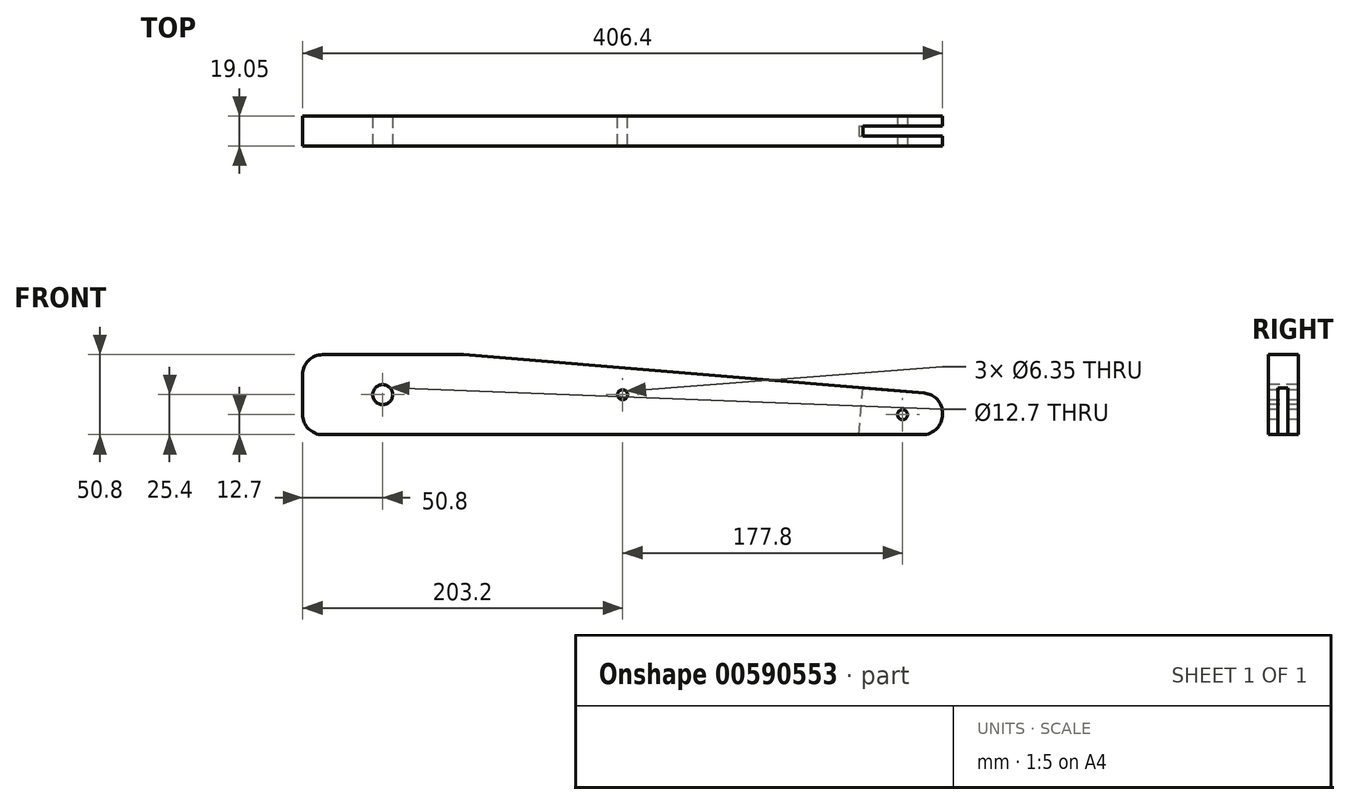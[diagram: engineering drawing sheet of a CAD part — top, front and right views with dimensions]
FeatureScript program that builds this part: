
annotation { "Feature Type Name" : "Feature", "Feature Type Description" : "" }
export const myFeature = defineFeature(function(context is Context, id is Id, definition is map)
    precondition{}
    {
        {
            var Q0;
            Q0=qCreatedBy(makeId("Front.planeOp"),FACE);
            var sketch = newSketch(context, id + "F0", { "sketchPlane" : qUnion([Q0])});
            skLineSegment(sketch, "E0.bottom", {"start": v(-203.2, 25.4) * mm, "end": v(203.2, 25.4) * mm});
            skLineSegment(sketch, "E0.top", {"start": v(-203.2, -25.4) * mm, "end": v(203.2, -25.4) * mm});
            skLineSegment(sketch, "E0.left", {"start": v(-203.2, 25.4) * mm, "end": v(-203.2, -25.4) * mm});
            skLineSegment(sketch, "E0.right", {"start": v(203.2, 25.4) * mm, "end": v(203.2, -25.4) * mm});
            skPoint(sketch, "E0.middle", {"position": v(0, 0) * mm});
            skCircle(sketch, "E1", {"center": v(0, 0) * mm, "radius": 3.18 * mm});
            skSolve(sketch);
        }
        {
            var Q0;
            Q0=makeQuery(id+"F0.imprint","IMPRINT",FACE,{"disambiguationData":[TD([[makeQuery(id+"F0.imprint","IMPRINT",EDGE,{"derivedFrom":sQuery(id+"F0.wireOp",EDGE,"E0.bottom")}),-1.0]])]});
            extrude(context, id + "F1", {"entities" : qUnion([Q0]), "depth" : 19.05 * mm, "offsetDistance" : 25.4 * mm});
        }
        {
            var Q0;
            Q0=makeQuery(id+"F1.opExtrude","SWEPT_EDGE",EDGE,{"disambiguationData":[OSD([sQuery(id+"F0.wireOp",EDGE,"E0.bottom"),sQuery(id+"F0.wireOp",EDGE,"E0.right")])]});
            chamfer(context, id + "F2", {"entities" : qUnion([Q0]), "chamferType" : ChamferType.TWO_OFFSETS, "width1" : 304.8 * mm, "oppositeDirection" : false, "width2" : 25.4 * mm, "tangentPropagation" : true});
        }
        {
            var Q0;
            Q0=makeQuery(id+"F1.opExtrude","CAP_FACE",FACE,{"disambiguationData":[OSD([sQuery(id+"F0.wireOp",EDGE,"E0.bottom"),sQuery(id+"F0.wireOp",EDGE,"E0.top"),sQuery(id+"F0.wireOp",EDGE,"E0.left"),sQuery(id+"F0.wireOp",EDGE,"E0.right")])],"isStart":false});
            var sketch = newSketch(context, id + "F3", { "sketchPlane" : qUnion([Q0])});
            skCircle(sketch, "E2", {"center": v(-152.4, 0) * mm, "radius": 6.35 * mm});
            skPoint(sketch, "E2.centerSnap0", {"position": v(-152.4, 25.4) * mm});
            skSolve(sketch);
        }
        {
            var Q0;
            Q0=makeQuery(id+"F3.imprint","IMPRINT",FACE,{"disambiguationData":[TD([[makeQuery(id+"F3.imprint","IMPRINT",EDGE,{"derivedFrom":sQuery(id+"F3.wireOp",EDGE,"E2")}),1.0]])]});
            extrude(context, id + "F4", {"entities" : qUnion([Q0]), "operationType" : NewBodyOperationType.REMOVE, "endBound" : BoundingType.THROUGH_ALL, "oppositeDirection" : true, "depth" : 25.4 * mm, "offsetDistance" : 25.4 * mm});
        }
        {
            var Q0;
            Q0=makeQuery(id+"F1.opExtrude","CAP_FACE",FACE,{"disambiguationData":[OSD([sQuery(id+"F0.wireOp",EDGE,"E0.bottom"),sQuery(id+"F0.wireOp",EDGE,"E0.top"),sQuery(id+"F0.wireOp",EDGE,"E0.left"),sQuery(id+"F0.wireOp",EDGE,"E0.right")])],"isStart":false});
            var sketch = newSketch(context, id + "F5", { "sketchPlane" : qUnion([Q0])});
            skCircle(sketch, "E3", {"center": v(177.8, -12.7) * mm, "radius": 3.18 * mm});
            skPoint(sketch, "E3.centerSnap0", {"position": v(203.2, -12.7) * mm});
            skSolve(sketch);
        }
        {
            var Q0;
            Q0=makeQuery(id+"F5.imprint","IMPRINT",FACE,{"disambiguationData":[TD([[makeQuery(id+"F5.imprint","IMPRINT",EDGE,{"derivedFrom":sQuery(id+"F5.wireOp",EDGE,"E3")}),1.0]])]});
            extrude(context, id + "F6", {"entities" : qUnion([Q0]), "operationType" : NewBodyOperationType.REMOVE, "endBound" : BoundingType.THROUGH_ALL, "oppositeDirection" : true, "depth" : 25.4 * mm, "offsetDistance" : 25.4 * mm});
        }
        {
            var Q0;
            Q0=makeQuery(id+"F2.opChamfer","BLEND_FACE",FACE,{"disambiguationData":[OSD([sQuery(id+"F0.wireOp",EDGE,"E0.bottom"),sQuery(id+"F0.wireOp",EDGE,"E0.right")])]});
            var sketch = newSketch(context, id + "F7", { "sketchPlane" : qUnion([Q0])});
            skLineSegment(sketch, "E4.bottom", {"start": v(151.7, -6.35) * mm, "end": v(202.5, -6.35) * mm});
            skLineSegment(sketch, "E4.top", {"start": v(151.7, -12.7) * mm, "end": v(202.5, -12.7) * mm});
            skLineSegment(sketch, "E4.left", {"start": v(151.7, -6.35) * mm, "end": v(151.7, -12.7) * mm});
            skLineSegment(sketch, "E4.right", {"start": v(202.5, -6.35) * mm, "end": v(202.5, -12.7) * mm});
            skSolve(sketch);
        }
        {
            var Q0;
            Q0=makeQuery(id+"F7.imprint","IMPRINT",FACE,{"disambiguationData":[TD([[makeQuery(id+"F7.imprint","IMPRINT",EDGE,{"derivedFrom":sQuery(id+"F7.wireOp",EDGE,"E4.bottom")}),-1.0]])]});
            extrude(context, id + "F8", {"entities" : qUnion([Q0]), "operationType" : NewBodyOperationType.REMOVE, "endBound" : BoundingType.THROUGH_ALL, "oppositeDirection" : true, "depth" : 25.4 * mm, "offsetDistance" : 25.4 * mm});
        }
        {
            var Q0;
            Q0=makeQuery(id+"F1.opExtrude","SWEPT_FACE",FACE,{"disambiguationData":[OSD([sQuery(id+"F0.wireOp",EDGE,"E0.right")])]});
            var sketch = newSketch(context, id + "F9", { "sketchPlane" : qUnion([Q0])});
            skLineSegment(sketch, "E5.bottom", {"start": v(-12.7, 0) * mm, "end": v(-6.35, 0) * mm});
            skLineSegment(sketch, "E5.top", {"start": v(-12.7, -25.4) * mm, "end": v(-6.35, -25.4) * mm});
            skLineSegment(sketch, "E5.left", {"start": v(-12.7, 0) * mm, "end": v(-12.7, -25.4) * mm});
            skLineSegment(sketch, "E5.right", {"start": v(-6.35, 0) * mm, "end": v(-6.35, -25.4) * mm});
            skSolve(sketch);
        }
        {
            var Q0;
            Q0=makeQuery(id+"F9.imprint","IMPRINT",FACE,{"disambiguationData":[TD([[makeQuery(id+"F9.imprint","IMPRINT",EDGE,{"derivedFrom":sQuery(id+"F9.wireOp",EDGE,"E5.bottom")}),1.0]])]});
            extrude(context, id + "F10", {"entities" : qUnion([Q0]), "operationType" : NewBodyOperationType.REMOVE, "oppositeDirection" : true, "depth" : 2.54 * mm, "offsetDistance" : 25.4 * mm});
        }
        {
            var Q0;
            Q0=makeQuery(id+"F1.opExtrude","SWEPT_EDGE",EDGE,{"disambiguationData":[OSD([sQuery(id+"F0.wireOp",EDGE,"E0.bottom"),sQuery(id+"F0.wireOp",EDGE,"E0.left")])]});
            var Q1;
            Q1=makeQuery(id+"F1.opExtrude","SWEPT_EDGE",EDGE,{"disambiguationData":[OSD([sQuery(id+"F0.wireOp",EDGE,"E0.top"),sQuery(id+"F0.wireOp",EDGE,"E0.left")])]});
            var Q2;
            {var subQ0=sQuery(id+"F0.wireOp",EDGE,"E0.right");var subQ1=sQuery(id+"F0.wireOp",EDGE,"E0.top");Q2=makeQuery(id+"F10.boolean.opBoolean","SPLIT",EDGE,{"disambiguationData":[TD([makeQuery(id+"F8.boolean.opBoolean","COPY",FACE,{"derivedFrom":makeQuery(id+"F8.opExtrude","SWEPT_FACE",FACE,{"disambiguationData":[OSD([sQuery(id+"F7.wireOp",EDGE,"E4.top")])]})})])],"derivedFrom":makeQuery(id+"F1.opExtrude","SWEPT_EDGE",EDGE,{"disambiguationData":[OSD([subQ1,subQ0])]})});}
            var Q3;
            {var subQ0=sQuery(id+"F0.wireOp",EDGE,"E0.right");var subQ1=sQuery(id+"F0.wireOp",EDGE,"E0.top");Q3=makeQuery(id+"F10.boolean.opBoolean","SPLIT",EDGE,{"disambiguationData":[TD([makeQuery(id+"F8.boolean.opBoolean","COPY",FACE,{"derivedFrom":makeQuery(id+"F8.opExtrude","SWEPT_FACE",FACE,{"disambiguationData":[OSD([sQuery(id+"F7.wireOp",EDGE,"E4.bottom")])]})})])],"derivedFrom":makeQuery(id+"F1.opExtrude","SWEPT_EDGE",EDGE,{"disambiguationData":[OSD([subQ1,subQ0])]})});}
            var Q4;
            {var subQ0=sQuery(id+"F0.wireOp",EDGE,"E0.right");var subQ1=sQuery(id+"F0.wireOp",EDGE,"E0.bottom");var subQ2=makeQuery(id+"F1.opExtrude","SWEPT_FACE",FACE,{"disambiguationData":[OSD([subQ0])]});Q4=makeQuery(id+"F8.boolean.opBoolean","SPLIT",EDGE,{"disambiguationData":[TD([makeQuery(id+"F8.opExtrude","SWEPT_FACE",FACE,{"disambiguationData":[OSD([sQuery(id+"F7.wireOp",EDGE,"E4.top")])]})])],"derivedFrom":makeQuery(id+"F2.opChamfer","BLEND_EDGE",EDGE,{"blendedFrom":[makeQuery(id+"F1.opExtrude","SWEPT_EDGE",EDGE,{"disambiguationData":[OSD([subQ1,subQ0])]}),subQ2],"blendedInto":[subQ2]})});}
            var Q5;
            {var subQ0=sQuery(id+"F0.wireOp",EDGE,"E0.right");var subQ1=sQuery(id+"F0.wireOp",EDGE,"E0.bottom");var subQ2=makeQuery(id+"F1.opExtrude","SWEPT_FACE",FACE,{"disambiguationData":[OSD([subQ0])]});Q5=makeQuery(id+"F8.boolean.opBoolean","SPLIT",EDGE,{"disambiguationData":[TD([makeQuery(id+"F8.opExtrude","SWEPT_FACE",FACE,{"disambiguationData":[OSD([sQuery(id+"F7.wireOp",EDGE,"E4.bottom")])]})])],"derivedFrom":makeQuery(id+"F2.opChamfer","BLEND_EDGE",EDGE,{"blendedFrom":[makeQuery(id+"F1.opExtrude","SWEPT_EDGE",EDGE,{"disambiguationData":[OSD([subQ1,subQ0])]}),subQ2],"blendedInto":[subQ2]})});}
            var Q6;
            {var subQ0=sQuery(id+"F0.wireOp",EDGE,"E0.bottom");Q6=makeQuery(id+"F2.opChamfer","BLEND_EDGE",EDGE,{"blendedFrom":[makeQuery(id+"F1.opExtrude","SWEPT_EDGE",EDGE,{"disambiguationData":[OSD([subQ0,sQuery(id+"F0.wireOp",EDGE,"E0.right")])]}),makeQuery(id+"F1.opExtrude","SWEPT_FACE",FACE,{"disambiguationData":[OSD([subQ0])]})],"blendedInto":[makeQuery(id+"F1.opExtrude","SWEPT_FACE",FACE,{"disambiguationData":[OSD([subQ0])]})]});}
            fillet(context, id + "F11", {"entities" : qUnion([Q0, Q1, Q2, Q3, Q4, Q5, Q6]), "radius" : 12.7 * mm, "tangentPropagation" : true, "allowEdgeOverflow" : false});
        }
    });
